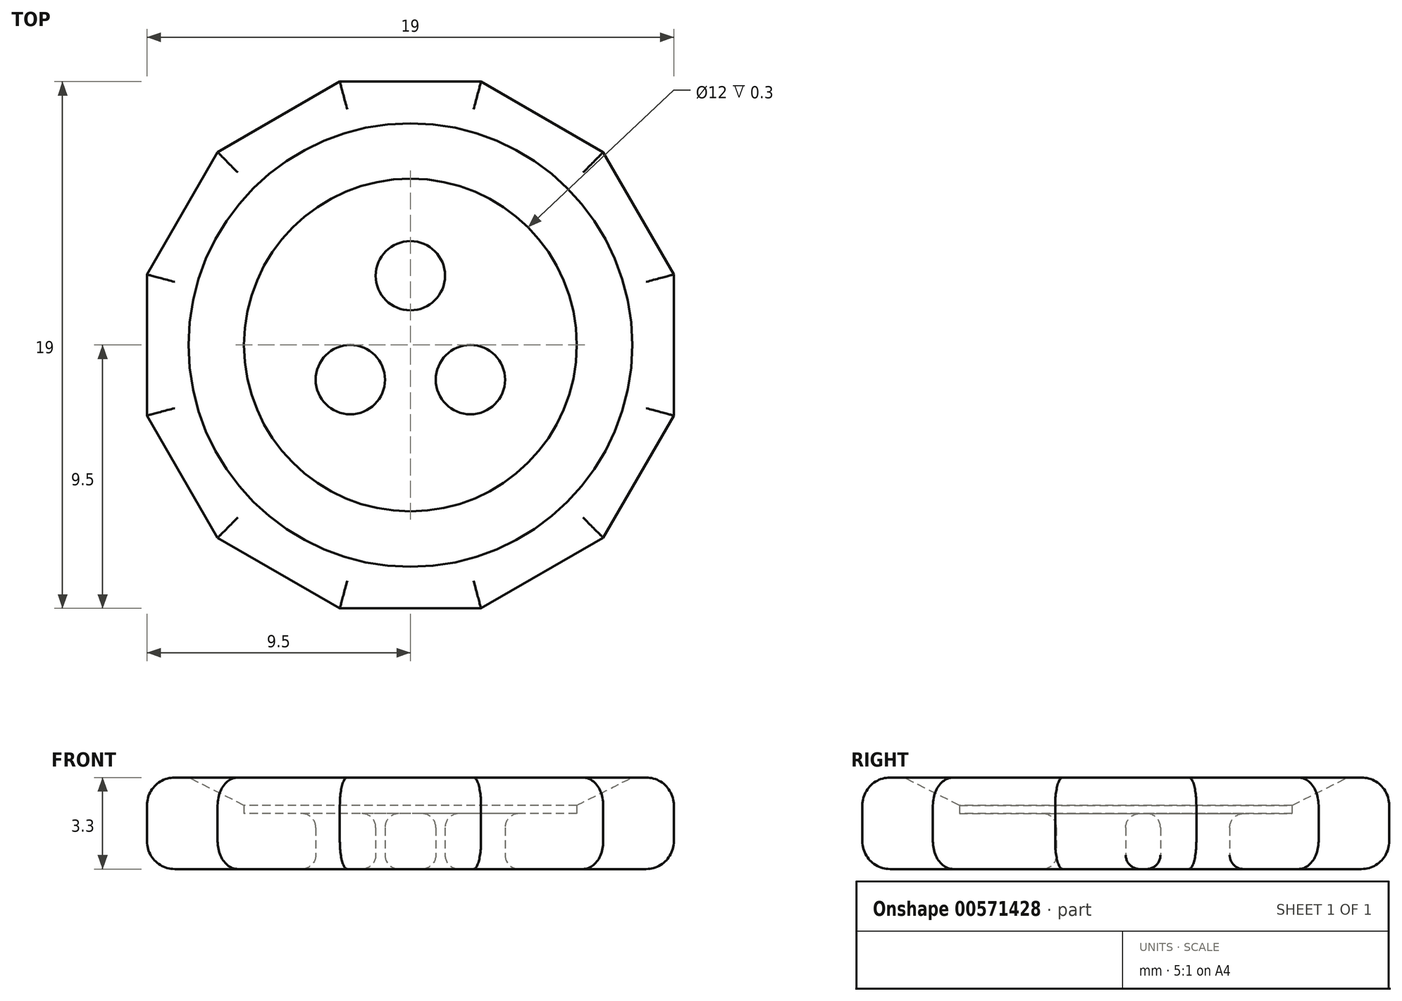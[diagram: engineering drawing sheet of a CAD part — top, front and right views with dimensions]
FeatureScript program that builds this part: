
annotation { "Feature Type Name" : "Feature", "Feature Type Description" : "" }
export const myFeature = defineFeature(function(context is Context, id is Id, definition is map)
    precondition{}
    {
        {
            var Q0;
            Q0=qCreatedBy(makeId("Top.planeOp"),FACE);
            var sketch = newSketch(context, id + "F0", { "sketchPlane" : qUnion([Q0])});
            skCircle(sketch, "E0", {"center": v(0, 0) * mm, "radius": 6 * mm});
            skCircle(sketch, "E1.cCircle", {"center": v(0, 0) * mm, "radius": 9.5 * mm, "construction": true});
            skLineSegment(sketch, "E1.0", {"start": v(-2.55, 9.5) * mm, "end": v(2.55, 9.5) * mm});
            skLineSegment(sketch, "E1.1", {"start": v(2.55, 9.5) * mm, "end": v(6.95, 6.95) * mm});
            skLineSegment(sketch, "E1.2", {"start": v(6.95, 6.95) * mm, "end": v(9.5, 2.55) * mm});
            skLineSegment(sketch, "E1.3", {"start": v(9.5, 2.55) * mm, "end": v(9.5, -2.55) * mm});
            skLineSegment(sketch, "E1.4", {"start": v(9.5, -2.55) * mm, "end": v(6.95, -6.95) * mm});
            skLineSegment(sketch, "E1.5", {"start": v(6.95, -6.95) * mm, "end": v(2.55, -9.5) * mm});
            skLineSegment(sketch, "E1.6", {"start": v(2.55, -9.5) * mm, "end": v(-2.55, -9.5) * mm});
            skLineSegment(sketch, "E1.7", {"start": v(-2.55, -9.5) * mm, "end": v(-6.95, -6.95) * mm});
            skLineSegment(sketch, "E1.8", {"start": v(-6.95, -6.95) * mm, "end": v(-9.5, -2.55) * mm});
            skLineSegment(sketch, "E1.9", {"start": v(-9.5, -2.55) * mm, "end": v(-9.5, 2.55) * mm});
            skLineSegment(sketch, "E1.10", {"start": v(-9.5, 2.55) * mm, "end": v(-6.95, 6.95) * mm});
            skLineSegment(sketch, "E1.11", {"start": v(-6.95, 6.95) * mm, "end": v(-2.55, 9.5) * mm});
            skPoint(sketch, "E1.0.midPoint", {"position": v(0, 9.5) * mm});
            skCircle(sketch, "E2", {"center": v(0, 2.5) * mm, "radius": 1.25 * mm});
            skCircle(sketch, "E3.1.0", {"center": v(-2.17, -1.25) * mm, "radius": 1.25 * mm});
            skCircle(sketch, "E3.2.0", {"center": v(2.17, -1.25) * mm, "radius": 1.25 * mm});
            skSolve(sketch);
        }
        {
            var Q0;
            Q0=makeQuery(id+"F0.imprint","IMPRINT",FACE,{"disambiguationData":[TD([[makeQuery(id+"F0.imprint","IMPRINT",EDGE,{"derivedFrom":sQuery(id+"F0.wireOp",EDGE,"E0")}),-1.0]])]});
            extrude(context, id + "F1", {"entities" : qUnion([Q0]), "depth" : 3.3 * mm, "offsetDistance" : 25 * mm});
        }
        {
            var Q0;
            Q0=makeQuery(id+"F0.imprint","IMPRINT",FACE,{"disambiguationData":[TD([[makeQuery(id+"F0.imprint","IMPRINT",EDGE,{"derivedFrom":sQuery(id+"F0.wireOp",EDGE,"E0")}),1.0]])]});
            extrude(context, id + "F2", {"entities" : qUnion([Q0]), "operationType" : NewBodyOperationType.ADD, "depth" : 2 * mm, "offsetDistance" : 25 * mm});
        }
        {
            var Q0;
            Q0=makeQuery(id+"F1.opExtrude","CAP_EDGE",EDGE,{"disambiguationData":[OSD([sQuery(id+"F0.wireOp",EDGE,"E1.8")])],"isStart":false});
            var Q1;
            Q1=makeQuery(id+"F1.opExtrude","CAP_EDGE",EDGE,{"disambiguationData":[OSD([sQuery(id+"F0.wireOp",EDGE,"E1.7")])],"isStart":false});
            var Q2;
            Q2=makeQuery(id+"F1.opExtrude","CAP_EDGE",EDGE,{"disambiguationData":[OSD([sQuery(id+"F0.wireOp",EDGE,"E1.6")])],"isStart":false});
            var Q3;
            Q3=makeQuery(id+"F1.opExtrude","CAP_EDGE",EDGE,{"disambiguationData":[OSD([sQuery(id+"F0.wireOp",EDGE,"E1.5")])],"isStart":false});
            var Q4;
            Q4=makeQuery(id+"F1.opExtrude","CAP_EDGE",EDGE,{"disambiguationData":[OSD([sQuery(id+"F0.wireOp",EDGE,"E1.4")])],"isStart":false});
            var Q5;
            Q5=makeQuery(id+"F1.opExtrude","CAP_EDGE",EDGE,{"disambiguationData":[OSD([sQuery(id+"F0.wireOp",EDGE,"E1.3")])],"isStart":false});
            var Q6;
            Q6=makeQuery(id+"F1.opExtrude","CAP_EDGE",EDGE,{"disambiguationData":[OSD([sQuery(id+"F0.wireOp",EDGE,"E1.2")])],"isStart":false});
            var Q7;
            Q7=makeQuery(id+"F1.opExtrude","CAP_EDGE",EDGE,{"disambiguationData":[OSD([sQuery(id+"F0.wireOp",EDGE,"E1.1")])],"isStart":false});
            var Q8;
            Q8=makeQuery(id+"F1.opExtrude","CAP_EDGE",EDGE,{"disambiguationData":[OSD([sQuery(id+"F0.wireOp",EDGE,"E1.0")])],"isStart":false});
            var Q9;
            Q9=makeQuery(id+"F1.opExtrude","CAP_EDGE",EDGE,{"disambiguationData":[OSD([sQuery(id+"F0.wireOp",EDGE,"E1.11")])],"isStart":false});
            var Q10;
            Q10=makeQuery(id+"F1.opExtrude","CAP_EDGE",EDGE,{"disambiguationData":[OSD([sQuery(id+"F0.wireOp",EDGE,"E1.10")])],"isStart":false});
            var Q11;
            Q11=makeQuery(id+"F1.opExtrude","CAP_EDGE",EDGE,{"disambiguationData":[OSD([sQuery(id+"F0.wireOp",EDGE,"E1.9")])],"isStart":false});
            var Q12;
            Q12=makeQuery(id+"F1.opExtrude","CAP_EDGE",EDGE,{"disambiguationData":[OSD([sQuery(id+"F0.wireOp",EDGE,"E1.8")])],"isStart":true});
            var Q13;
            Q13=makeQuery(id+"F1.opExtrude","CAP_EDGE",EDGE,{"disambiguationData":[OSD([sQuery(id+"F0.wireOp",EDGE,"E1.7")])],"isStart":true});
            var Q14;
            Q14=makeQuery(id+"F1.opExtrude","CAP_EDGE",EDGE,{"disambiguationData":[OSD([sQuery(id+"F0.wireOp",EDGE,"E1.6")])],"isStart":true});
            var Q15;
            Q15=makeQuery(id+"F1.opExtrude","CAP_EDGE",EDGE,{"disambiguationData":[OSD([sQuery(id+"F0.wireOp",EDGE,"E1.5")])],"isStart":true});
            var Q16;
            Q16=makeQuery(id+"F1.opExtrude","CAP_EDGE",EDGE,{"disambiguationData":[OSD([sQuery(id+"F0.wireOp",EDGE,"E1.4")])],"isStart":true});
            var Q17;
            Q17=makeQuery(id+"F1.opExtrude","CAP_EDGE",EDGE,{"disambiguationData":[OSD([sQuery(id+"F0.wireOp",EDGE,"E1.3")])],"isStart":true});
            var Q18;
            Q18=makeQuery(id+"F1.opExtrude","CAP_EDGE",EDGE,{"disambiguationData":[OSD([sQuery(id+"F0.wireOp",EDGE,"E1.2")])],"isStart":true});
            var Q19;
            Q19=makeQuery(id+"F1.opExtrude","CAP_EDGE",EDGE,{"disambiguationData":[OSD([sQuery(id+"F0.wireOp",EDGE,"E1.1")])],"isStart":true});
            var Q20;
            Q20=makeQuery(id+"F1.opExtrude","CAP_EDGE",EDGE,{"disambiguationData":[OSD([sQuery(id+"F0.wireOp",EDGE,"E1.0")])],"isStart":true});
            var Q21;
            Q21=makeQuery(id+"F1.opExtrude","CAP_EDGE",EDGE,{"disambiguationData":[OSD([sQuery(id+"F0.wireOp",EDGE,"E1.11")])],"isStart":true});
            var Q22;
            Q22=makeQuery(id+"F1.opExtrude","CAP_EDGE",EDGE,{"disambiguationData":[OSD([sQuery(id+"F0.wireOp",EDGE,"E1.10")])],"isStart":true});
            var Q23;
            Q23=makeQuery(id+"F1.opExtrude","CAP_EDGE",EDGE,{"disambiguationData":[OSD([sQuery(id+"F0.wireOp",EDGE,"E1.9")])],"isStart":true});
            fillet(context, id + "F3", {"entities" : qUnion([Q0, Q1, Q2, Q3, Q4, Q5, Q6, Q7, Q8, Q9, Q10, Q11, Q12, Q13, Q14, Q15, Q16, Q17, Q18, Q19, Q20, Q21, Q22, Q23]), "radius" : 1 * mm, "tangentPropagation" : true, "allowEdgeOverflow" : false});
        }
        {
            var Q0;
            Q0=makeQuery(id+"F1.opExtrude","CAP_EDGE",EDGE,{"disambiguationData":[OSD([sQuery(id+"F0.wireOp",EDGE,"E0")])],"isStart":false});
            chamfer(context, id + "F4", {"entities" : qUnion([Q0]), "chamferType" : ChamferType.TWO_OFFSETS, "width1" : 1 * mm, "oppositeDirection" : false, "width2" : 2 * mm, "tangentPropagation" : true});
        }
        {
            var Q0;
            Q0=makeQuery(id+"F2.opExtrude","CAP_EDGE",EDGE,{"disambiguationData":[OSD([sQuery(id+"F0.wireOp",EDGE,"E2")])],"isStart":false});
            var Q1;
            Q1=makeQuery(id+"F2.opExtrude","CAP_EDGE",EDGE,{"disambiguationData":[OSD([sQuery(id+"F0.wireOp",EDGE,"E3.2.0")])],"isStart":false});
            var Q2;
            Q2=makeQuery(id+"F2.opExtrude","CAP_EDGE",EDGE,{"disambiguationData":[OSD([sQuery(id+"F0.wireOp",EDGE,"E3.1.0")])],"isStart":false});
            var Q3;
            Q3=makeQuery(id+"F2.opExtrude","CAP_EDGE",EDGE,{"disambiguationData":[OSD([sQuery(id+"F0.wireOp",EDGE,"E3.2.0")])],"isStart":true});
            var Q4;
            Q4=makeQuery(id+"F2.opExtrude","CAP_EDGE",EDGE,{"disambiguationData":[OSD([sQuery(id+"F0.wireOp",EDGE,"E3.1.0")])],"isStart":true});
            var Q5;
            Q5=makeQuery(id+"F2.opExtrude","CAP_EDGE",EDGE,{"disambiguationData":[OSD([sQuery(id+"F0.wireOp",EDGE,"E2")])],"isStart":true});
            fillet(context, id + "F5", {"entities" : qUnion([Q0, Q1, Q2, Q3, Q4, Q5]), "radius" : 0.5 * mm, "tangentPropagation" : true, "allowEdgeOverflow" : false});
        }
    });
